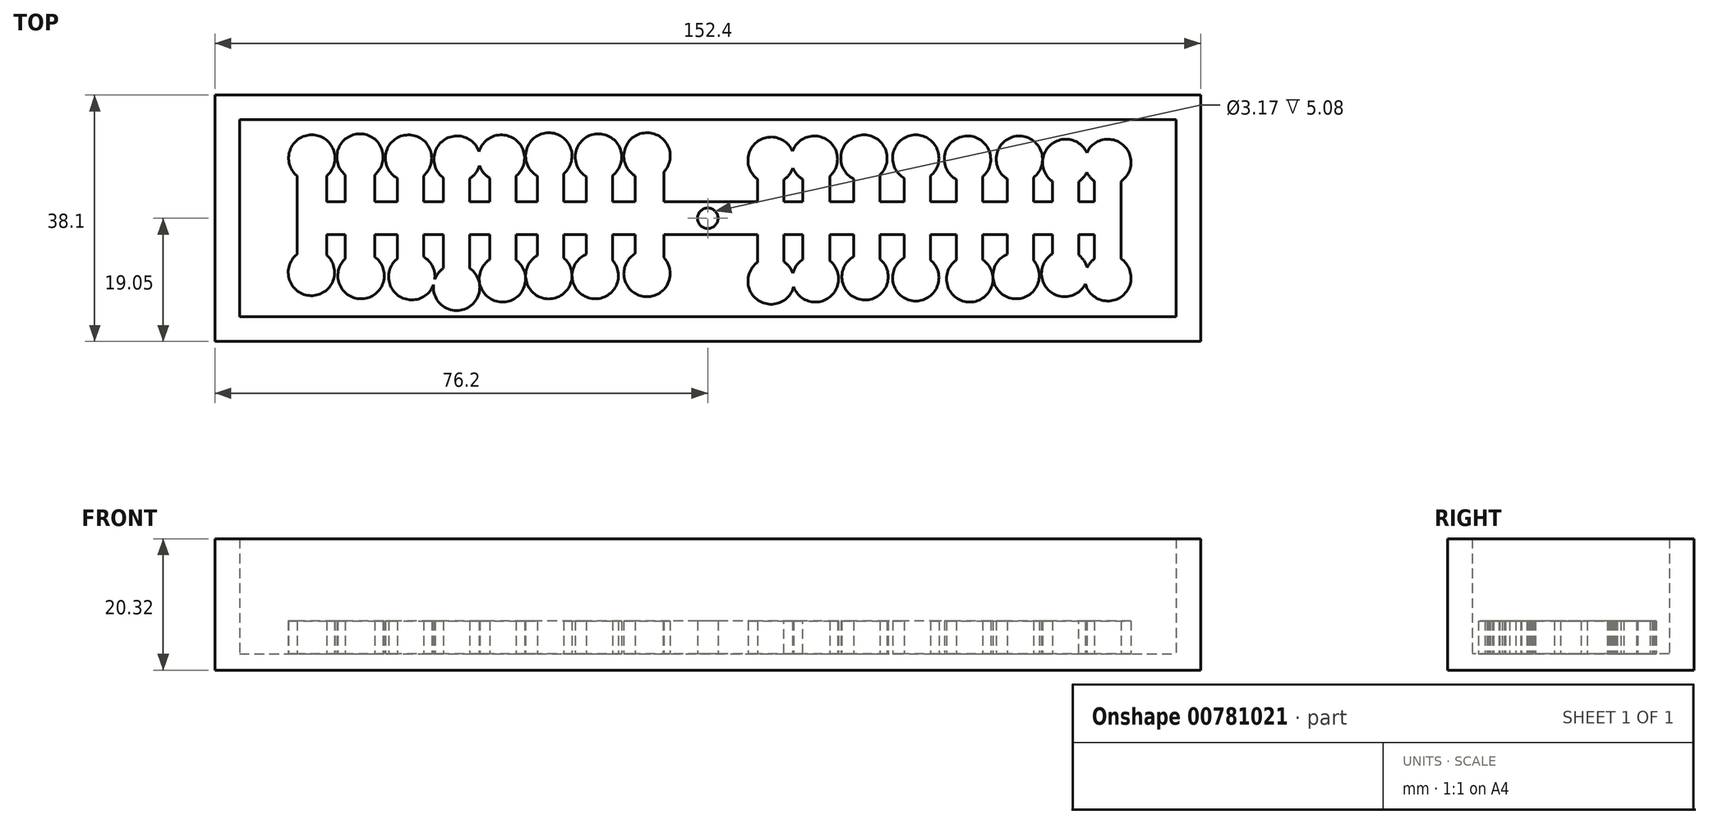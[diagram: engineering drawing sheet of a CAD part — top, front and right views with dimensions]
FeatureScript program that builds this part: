
annotation { "Feature Type Name" : "Feature", "Feature Type Description" : "" }
export const myFeature = defineFeature(function(context is Context, id is Id, definition is map)
    precondition{}
    {
        {
            var Q0;
            Q0=qCreatedBy(makeId("Top.planeOp"),FACE);
            var sketch = newSketch(context, id + "F0", { "sketchPlane" : qUnion([Q0])});
            skLineSegment(sketch, "E0.bottom", {"start": v(76.2, -19.05) * mm, "end": v(-76.2, -19.05) * mm});
            skLineSegment(sketch, "E0.top", {"start": v(76.2, 19.05) * mm, "end": v(-76.2, 19.05) * mm});
            skLineSegment(sketch, "E0.left", {"start": v(76.2, -19.05) * mm, "end": v(76.2, 19.05) * mm});
            skLineSegment(sketch, "E0.right", {"start": v(-76.2, -19.05) * mm, "end": v(-76.2, 19.05) * mm});
            skPoint(sketch, "E0.middle", {"position": v(0, 0) * mm});
            skLineSegment(sketch, "E1.bottom", {"start": v(-76.2, 19.05) * mm, "end": v(76.2, 19.05) * mm});
            skLineSegment(sketch, "E1.top", {"start": v(-76.2, 15.24) * mm, "end": v(76.2, 15.24) * mm});
            skLineSegment(sketch, "E1.left", {"start": v(-76.2, 19.05) * mm, "end": v(-76.2, 15.24) * mm});
            skLineSegment(sketch, "E1.right", {"start": v(76.2, 19.05) * mm, "end": v(76.2, 15.24) * mm});
            skLineSegment(sketch, "E2.bottom", {"start": v(-76.2, 19.05) * mm, "end": v(-72.39, 19.05) * mm});
            skLineSegment(sketch, "E2.top", {"start": v(-76.2, -19.05) * mm, "end": v(-72.39, -19.05) * mm});
            skLineSegment(sketch, "E2.left", {"start": v(-76.2, 19.05) * mm, "end": v(-76.2, -19.05) * mm});
            skLineSegment(sketch, "E2.right", {"start": v(-72.39, 19.05) * mm, "end": v(-72.39, -19.05) * mm});
            skLineSegment(sketch, "E3.bottom", {"start": v(-76.2, -19.05) * mm, "end": v(76.2, -19.05) * mm});
            skLineSegment(sketch, "E3.top", {"start": v(-76.2, -15.24) * mm, "end": v(76.2, -15.24) * mm});
            skLineSegment(sketch, "E3.left", {"start": v(-76.2, -19.05) * mm, "end": v(-76.2, -15.24) * mm});
            skLineSegment(sketch, "E3.right", {"start": v(76.2, -19.05) * mm, "end": v(76.2, -15.24) * mm});
            skLineSegment(sketch, "E4.bottom", {"start": v(72.4, 19.05) * mm, "end": v(76.2, 19.05) * mm});
            skLineSegment(sketch, "E4.top", {"start": v(72.4, -19.05) * mm, "end": v(76.2, -19.05) * mm});
            skLineSegment(sketch, "E4.left", {"start": v(72.4, 19.05) * mm, "end": v(72.4, -19.05) * mm});
            skLineSegment(sketch, "E4.right", {"start": v(76.2, 19.05) * mm, "end": v(76.2, -19.05) * mm});
            skSolve(sketch);
        }
        {
            var Q0;
            Q0=qCreatedBy(makeId("Top.planeOp"),FACE);
            var sketch = newSketch(context, id + "F1", { "sketchPlane" : qUnion([Q0])});
            skLineSegment(sketch, "E5.bottom", {"start": v(-76.2, -19.05) * mm, "end": v(76.2, -19.05) * mm});
            skLineSegment(sketch, "E5.top", {"start": v(-76.2, 19.05) * mm, "end": v(76.2, 19.05) * mm});
            skLineSegment(sketch, "E5.left", {"start": v(-76.2, -19.05) * mm, "end": v(-76.2, 19.05) * mm});
            skLineSegment(sketch, "E5.right", {"start": v(76.2, -19.05) * mm, "end": v(76.2, 19.05) * mm});
            skSolve(sketch);
        }
        {
            var Q0;
            Q0 = qSketchRegion(id + "F1", true);
            extrude(context, id + "F2", {"entities" : qUnion([Q0]), "oppositeDirection" : true, "depth" : 2.54 * mm, "offsetDistance" : 25.4 * mm});
        }
        {
            var Q0;
            {var subQ0=sQuery(id+"F0.wireOp",EDGE,"E0.right");var subQ1=sQuery(id+"F0.wireOp",EDGE,"E0.top");var subQ2=makeQuery(id+"F0.imprint","INTERSECT",VERTEX,{"derivedFrom":[subQ1,subQ0]});var subQ10=sQuery(id+"F0.wireOp",EDGE,"E4.left");var subQ11=makeQuery(id+"F0.imprint","INTERSECT",VERTEX,{"derivedFrom":[subQ1,subQ10]});var subQ14=sQuery(id+"F0.wireOp",EDGE,"E0.bottom");var subQ15=makeQuery(id+"F0.imprint","INTERSECT",VERTEX,{"derivedFrom":[subQ14,subQ10]});var subQ16=sQuery(id+"F0.wireOp",EDGE,"E0.left");var subQ18=sQuery(id+"F0.wireOp",EDGE,"E3.top");var subQ19=makeQuery(id+"F0.imprint","INTERSECT",VERTEX,{"derivedFrom":[subQ16,subQ18]});var subQ23=makeQuery(id+"F0.imprint","INTERSECT",VERTEX,{"derivedFrom":[subQ0,subQ18]});var subQ28=makeQuery(id+"F0.imprint","INTERSECT",VERTEX,{"derivedFrom":[subQ14,subQ0]});Q0=qUnion([makeQuery(id+"F0.imprint","IMPRINT",FACE,{"disambiguationData":[TD([[makeQuery(id+"F0.imprint","IMPRINT",EDGE,{"disambiguationData":[TD([[subQ11,1.0]])],"derivedFrom":subQ1}),1.0]])]}),makeQuery(id+"F0.imprint","IMPRINT",FACE,{"disambiguationData":[TD([[makeQuery(id+"F0.imprint","IMPRINT",EDGE,{"disambiguationData":[TD([[subQ19,-1.0]])],"derivedFrom":subQ16}),1.0]])]}),makeQuery(id+"F0.imprint","IMPRINT",FACE,{"disambiguationData":[TD([[makeQuery(id+"F0.imprint","IMPRINT",EDGE,{"disambiguationData":[TD([[subQ28,1.0]])],"derivedFrom":subQ14}),-1.0]])]}),makeQuery(id+"F0.imprint","IMPRINT",FACE,{"disambiguationData":[TD([[makeQuery(id+"F0.imprint","IMPRINT",EDGE,{"disambiguationData":[TD([[subQ15,-1.0]])],"derivedFrom":subQ14}),-1.0]])]}),makeQuery(id+"F0.imprint","IMPRINT",FACE,{"disambiguationData":[TD([[makeQuery(id+"F0.imprint","IMPRINT",EDGE,{"disambiguationData":[TD([[subQ23,-1.0]])],"derivedFrom":subQ0}),-1.0]])]}),makeQuery(id+"F0.imprint","IMPRINT",FACE,{"disambiguationData":[TD([[makeQuery(id+"F0.imprint","IMPRINT",EDGE,{"disambiguationData":[TD([[subQ15,1.0]])],"derivedFrom":subQ14}),-1.0]])]}),makeQuery(id+"F0.imprint","IMPRINT",FACE,{"disambiguationData":[TD([[makeQuery(id+"F0.imprint","IMPRINT",EDGE,{"disambiguationData":[TD([[subQ11,-1.0]])],"derivedFrom":subQ1}),1.0]])]}),makeQuery(id+"F0.imprint","IMPRINT",FACE,{"disambiguationData":[TD([[makeQuery(id+"F0.imprint","IMPRINT",EDGE,{"disambiguationData":[TD([[subQ2,1.0]])],"derivedFrom":subQ1}),1.0]])]})]);}
            var Q1;
            Q1=makeQuery(id+"F0.imprint","IMPRINT",FACE,{"disambiguationData":[TD([[makeQuery(id+"F0.imprint","IMPRINT",EDGE,{"derivedFrom":sQuery(id+"F0.wireOp",EDGE,"pY6SBwOU-86oe-tOPr-FGqK-fUqq77zkzXOc")}),1.0]])]});
            extrude(context, id + "F3", {"entities" : qUnion([Q0, Q1]), "operationType" : NewBodyOperationType.ADD, "depth" : 17.78 * mm, "offsetDistance" : 25.4 * mm});
        }
        {
            var Q0;
            Q0=qCreatedBy(makeId("Top.planeOp"),FACE);
            var sketch = newSketch(context, id + "F4", { "sketchPlane" : qUnion([Q0])});
            skLineSegment(sketch, "E6.bottom", {"start": v(63.5, -2.54) * mm, "end": v(-63.5, -2.54) * mm});
            skLineSegment(sketch, "E6.top", {"start": v(63.5, 2.54) * mm, "end": v(-63.5, 2.54) * mm});
            skLineSegment(sketch, "E6.left", {"start": v(63.5, -2.54) * mm, "end": v(63.5, 2.54) * mm});
            skLineSegment(sketch, "E6.right", {"start": v(-63.5, -2.54) * mm, "end": v(-63.5, 2.54) * mm});
            skPoint(sketch, "E6.middle", {"position": v(0, 0) * mm});
            skLineSegment(sketch, "E7.bottom", {"start": v(-63.5, 10.86) * mm, "end": v(-58.93, 10.86) * mm});
            skLineSegment(sketch, "E7.top", {"start": v(-63.5, -10.59) * mm, "end": v(-58.93, -10.59) * mm});
            skLineSegment(sketch, "E7.left", {"start": v(-63.5, 10.86) * mm, "end": v(-63.5, -10.59) * mm});
            skLineSegment(sketch, "E7.right", {"start": v(-58.93, 10.86) * mm, "end": v(-58.93, -10.59) * mm});
            skLineSegment(sketch, "E8.bottom", {"start": v(-48.01, 10.68) * mm, "end": v(-43.95, 10.68) * mm});
            skLineSegment(sketch, "E8.top", {"start": v(-48.01, -10.59) * mm, "end": v(-43.95, -10.59) * mm});
            skLineSegment(sketch, "E8.left", {"start": v(-48.01, 10.68) * mm, "end": v(-48.01, -10.59) * mm});
            skLineSegment(sketch, "E8.right", {"start": v(-43.95, 10.68) * mm, "end": v(-43.95, -10.59) * mm});
            skLineSegment(sketch, "E9.bottom", {"start": v(-40.87, 10.77) * mm, "end": v(-36.8, 10.77) * mm});
            skLineSegment(sketch, "E9.top", {"start": v(-40.87, -10.67) * mm, "end": v(-36.8, -10.67) * mm});
            skLineSegment(sketch, "E9.left", {"start": v(-40.87, 10.77) * mm, "end": v(-40.87, -10.67) * mm});
            skLineSegment(sketch, "E9.right", {"start": v(-36.8, 10.77) * mm, "end": v(-36.8, -10.67) * mm});
            skLineSegment(sketch, "E10.bottom", {"start": v(30.36, 10.1) * mm, "end": v(34.43, 10.1) * mm});
            skLineSegment(sketch, "E10.top", {"start": v(30.36, -11.18) * mm, "end": v(34.43, -11.18) * mm});
            skLineSegment(sketch, "E10.left", {"start": v(30.36, 10.1) * mm, "end": v(30.36, -11.18) * mm});
            skLineSegment(sketch, "E10.right", {"start": v(34.43, 10.1) * mm, "end": v(34.43, -11.18) * mm});
            skLineSegment(sketch, "E11.bottom", {"start": v(38.43, 10.12) * mm, "end": v(42.5, 10.12) * mm});
            skLineSegment(sketch, "E11.top", {"start": v(38.43, -11.16) * mm, "end": v(42.5, -11.16) * mm});
            skLineSegment(sketch, "E11.left", {"start": v(38.43, 10.12) * mm, "end": v(38.43, -11.16) * mm});
            skLineSegment(sketch, "E11.right", {"start": v(42.5, 10.12) * mm, "end": v(42.5, -11.16) * mm});
            skLineSegment(sketch, "E12.bottom", {"start": v(-33.7, 10.77) * mm, "end": v(-29.62, 10.77) * mm});
            skLineSegment(sketch, "E12.top", {"start": v(-33.7, -10.67) * mm, "end": v(-29.62, -10.67) * mm});
            skLineSegment(sketch, "E12.left", {"start": v(-33.7, 10.77) * mm, "end": v(-33.7, -10.67) * mm});
            skLineSegment(sketch, "E12.right", {"start": v(-29.62, 10.77) * mm, "end": v(-29.62, -10.67) * mm});
            skLineSegment(sketch, "E13.bottom", {"start": v(22.56, 10.17) * mm, "end": v(26.62, 10.17) * mm});
            skLineSegment(sketch, "E13.top", {"start": v(22.56, -10.76) * mm, "end": v(26.62, -10.76) * mm});
            skLineSegment(sketch, "E13.left", {"start": v(22.56, 10.17) * mm, "end": v(22.56, -10.76) * mm});
            skLineSegment(sketch, "E13.right", {"start": v(26.62, 10.17) * mm, "end": v(26.62, -10.76) * mm});
            skLineSegment(sketch, "E14.bottom", {"start": v(-26.34, 10.77) * mm, "end": v(-22.27, 10.77) * mm});
            skLineSegment(sketch, "E14.top", {"start": v(-26.34, -10.67) * mm, "end": v(-22.27, -10.67) * mm});
            skLineSegment(sketch, "E14.left", {"start": v(-26.34, 10.77) * mm, "end": v(-26.34, -10.67) * mm});
            skLineSegment(sketch, "E14.right", {"start": v(-22.27, 10.77) * mm, "end": v(-22.27, -10.67) * mm});
            skLineSegment(sketch, "E15.bottom", {"start": v(-18.78, 10.6) * mm, "end": v(-14.72, 10.6) * mm});
            skLineSegment(sketch, "E15.top", {"start": v(-18.78, -10.85) * mm, "end": v(-14.72, -10.85) * mm});
            skLineSegment(sketch, "E15.left", {"start": v(-18.78, 10.6) * mm, "end": v(-18.78, -10.85) * mm});
            skLineSegment(sketch, "E15.right", {"start": v(-14.72, 10.6) * mm, "end": v(-14.72, -10.85) * mm});
            skLineSegment(sketch, "E16.bottom", {"start": v(-11.2, 10.68) * mm, "end": v(-6.8, 10.68) * mm});
            skLineSegment(sketch, "E16.top", {"start": v(-11.2, -11.1) * mm, "end": v(-6.8, -11.1) * mm});
            skLineSegment(sketch, "E16.left", {"start": v(-11.2, 10.68) * mm, "end": v(-11.2, -11.1) * mm});
            skLineSegment(sketch, "E16.right", {"start": v(-6.8, 10.68) * mm, "end": v(-6.8, -11.1) * mm});
            skLineSegment(sketch, "E17.bottom", {"start": v(7.7, 10.34) * mm, "end": v(11.76, 10.34) * mm});
            skLineSegment(sketch, "E17.top", {"start": v(7.7, -11.1) * mm, "end": v(11.76, -11.1) * mm});
            skLineSegment(sketch, "E17.left", {"start": v(7.7, 10.34) * mm, "end": v(7.7, -11.1) * mm});
            skLineSegment(sketch, "E17.right", {"start": v(11.76, 10.34) * mm, "end": v(11.76, -11.1) * mm});
            skLineSegment(sketch, "E18.bottom", {"start": v(14.67, 10.3) * mm, "end": v(18.9, 10.3) * mm});
            skLineSegment(sketch, "E18.top", {"start": v(14.67, -10.98) * mm, "end": v(18.9, -10.98) * mm});
            skLineSegment(sketch, "E18.left", {"start": v(14.67, 10.3) * mm, "end": v(14.67, -10.98) * mm});
            skLineSegment(sketch, "E18.right", {"start": v(18.9, 10.3) * mm, "end": v(18.9, -10.98) * mm});
            skLineSegment(sketch, "E19.bottom", {"start": v(46.3, 10.18) * mm, "end": v(50.37, 10.18) * mm});
            skLineSegment(sketch, "E19.top", {"start": v(46.3, -10.77) * mm, "end": v(50.37, -10.77) * mm});
            skLineSegment(sketch, "E19.left", {"start": v(46.3, 10.18) * mm, "end": v(46.3, -10.77) * mm});
            skLineSegment(sketch, "E19.right", {"start": v(50.37, 10.18) * mm, "end": v(50.37, -10.77) * mm});
            skLineSegment(sketch, "E20.bottom", {"start": v(53.29, 9.68) * mm, "end": v(57.35, 9.68) * mm});
            skLineSegment(sketch, "E20.top", {"start": v(53.29, -10.93) * mm, "end": v(57.35, -10.93) * mm});
            skLineSegment(sketch, "E20.left", {"start": v(53.29, 9.68) * mm, "end": v(53.29, -10.93) * mm});
            skLineSegment(sketch, "E20.right", {"start": v(57.35, 9.68) * mm, "end": v(57.35, -10.93) * mm});
            skLineSegment(sketch, "E21.bottom", {"start": v(59.8, 9.85) * mm, "end": v(63.87, 9.85) * mm});
            skLineSegment(sketch, "E21.top", {"start": v(59.8, -10.93) * mm, "end": v(63.87, -10.93) * mm});
            skLineSegment(sketch, "E21.left", {"start": v(59.8, 9.85) * mm, "end": v(59.8, -10.93) * mm});
            skLineSegment(sketch, "E21.right", {"start": v(63.87, 9.85) * mm, "end": v(63.87, -10.93) * mm});
            skCircle(sketch, "E22", {"center": v(0, 0) * mm, "radius": 1.59 * mm});
            skLineSegment(sketch, "E23.bottom", {"start": v(-56.05, 10.7) * mm, "end": v(-51.49, 10.7) * mm});
            skLineSegment(sketch, "E23.top", {"start": v(-56.05, -10.75) * mm, "end": v(-51.49, -10.75) * mm});
            skLineSegment(sketch, "E23.left", {"start": v(-56.05, 10.7) * mm, "end": v(-56.05, -10.75) * mm});
            skLineSegment(sketch, "E23.right", {"start": v(-51.49, 10.7) * mm, "end": v(-51.49, -10.75) * mm});
            skCircle(sketch, "E24", {"center": v(-61.22, 9.32) * mm, "radius": 3.58 * mm});
            skPoint(sketch, "E24.centerSnap0", {"position": v(-61.22, 10.86) * mm});
            skCircle(sketch, "E25", {"center": v(-61.28, -8.37) * mm, "radius": 3.58 * mm});
            skCircle(sketch, "E26", {"center": v(-53.77, 9.48) * mm, "radius": 3.58 * mm});
            skCircle(sketch, "E27", {"center": v(-53.6, -8.87) * mm, "radius": 3.58 * mm});
            skCircle(sketch, "E28", {"center": v(-46.26, 9.32) * mm, "radius": 3.58 * mm});
            skCircle(sketch, "E29", {"center": v(-45.76, -9.04) * mm, "radius": 3.58 * mm});
            skCircle(sketch, "E30", {"center": v(-38.75, 9.15) * mm, "radius": 3.58 * mm});
            skCircle(sketch, "E31", {"center": v(-31.91, 9.32) * mm, "radius": 3.58 * mm});
            skCircle(sketch, "E32", {"center": v(-31.75, -9.37) * mm, "radius": 3.58 * mm});
            skCircle(sketch, "E33", {"center": v(-24.57, 9.65) * mm, "radius": 3.58 * mm});
            skCircle(sketch, "E34", {"center": v(-24.57, -8.87) * mm, "radius": 3.58 * mm});
            skCircle(sketch, "E35", {"center": v(-16.9, 9.48) * mm, "radius": 3.58 * mm});
            skCircle(sketch, "E36", {"center": v(-17.4, -8.87) * mm, "radius": 3.58 * mm});
            skCircle(sketch, "E37", {"center": v(-9.39, 9.65) * mm, "radius": 3.58 * mm});
            skCircle(sketch, "E38", {"center": v(-9.39, -8.54) * mm, "radius": 3.58 * mm});
            skCircle(sketch, "E39", {"center": v(9.8, 8.98) * mm, "radius": 3.58 * mm});
            skCircle(sketch, "E40", {"center": v(9.8, -9.7) * mm, "radius": 3.58 * mm});
            skCircle(sketch, "E41", {"center": v(16.47, 9.15) * mm, "radius": 3.58 * mm});
            skCircle(sketch, "E42", {"center": v(16.64, -9.37) * mm, "radius": 3.58 * mm});
            skCircle(sketch, "E43", {"center": v(24.15, 9.32) * mm, "radius": 3.58 * mm});
            skCircle(sketch, "E44", {"center": v(32.16, -9.2) * mm, "radius": 3.58 * mm});
            skCircle(sketch, "E45", {"center": v(24.31, -9.04) * mm, "radius": 3.58 * mm});
            skCircle(sketch, "E46", {"center": v(32.16, 9.32) * mm, "radius": 3.58 * mm});
            skCircle(sketch, "E47", {"center": v(40.5, -9.37) * mm, "radius": 3.58 * mm});
            skCircle(sketch, "E48", {"center": v(48.17, 9.15) * mm, "radius": 3.58 * mm});
            skCircle(sketch, "E49", {"center": v(40.16, 9.15) * mm, "radius": 3.58 * mm});
            skCircle(sketch, "E50", {"center": v(61.85, 8.65) * mm, "radius": 3.58 * mm});
            skCircle(sketch, "E51", {"center": v(47.67, -8.87) * mm, "radius": 3.58 * mm});
            skCircle(sketch, "E52", {"center": v(61.85, -9.2) * mm, "radius": 3.58 * mm});
            skCircle(sketch, "E53", {"center": v(55.18, -8.54) * mm, "radius": 3.58 * mm});
            skCircle(sketch, "E54", {"center": v(55.35, 8.65) * mm, "radius": 3.58 * mm});
            skCircle(sketch, "E55", {"center": v(-38.83, -10.67) * mm, "radius": 3.58 * mm});
            skSolve(sketch);
        }
        {
            var Q0;
            Q0=makeQuery(id+"F4.imprint","IMPRINT",FACE,{"disambiguationData":[TD([[makeQuery(id+"F4.imprint","IMPRINT",EDGE,{"derivedFrom":sQuery(id+"F4.wireOp",EDGE,"E6.bottom")}),-1.0]])]});
            extrude(context, id + "F5", {"entities" : qUnion([Q0]), "operationType" : NewBodyOperationType.ADD, "depth" : 5.08 * mm, "offsetDistance" : 25.4 * mm});
        }
        {
            var Q0;
            Q0 = qSketchRegion(id + "F4", true);
            extrude(context, id + "F6", {"entities" : qUnion([Q0]), "operationType" : NewBodyOperationType.ADD, "depth" : 5.08 * mm, "offsetDistance" : 25.4 * mm});
        }
    });
